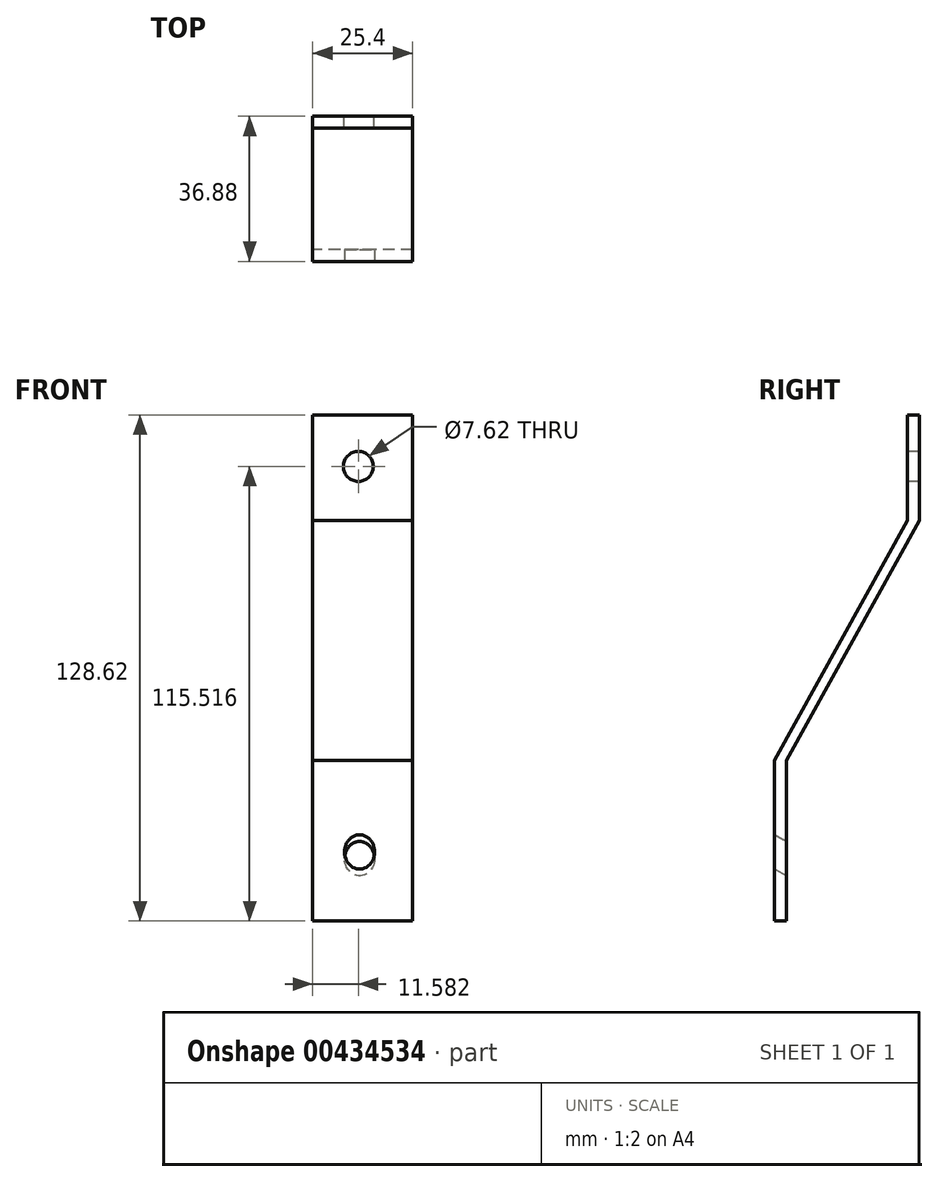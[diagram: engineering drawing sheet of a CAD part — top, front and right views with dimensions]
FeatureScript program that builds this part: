
annotation { "Feature Type Name" : "Feature", "Feature Type Description" : "" }
export const myFeature = defineFeature(function(context is Context, id is Id, definition is map)
    precondition{}
    {
        {
            var Q0;
            Q0=qCreatedBy(makeId("Right.planeOp"),FACE);
            var sketch = newSketch(context, id + "F0", { "sketchPlane" : qUnion([Q0])});
            skLineSegment(sketch, "E0.bottom", {"start": v(-49.07, -10.82) * mm, "end": v(-46.02, -10.82) * mm});
            skLineSegment(sketch, "E0.top", {"start": v(-49.07, -51.66) * mm, "end": v(-46.02, -51.66) * mm});
            skLineSegment(sketch, "E0.left", {"start": v(-49.07, -10.82) * mm, "end": v(-49.07, -51.66) * mm});
            skLineSegment(sketch, "E0.right", {"start": v(-46.02, -10.82) * mm, "end": v(-46.02, -51.66) * mm});
            skPoint(sketch, "E0.middle", {"position": v(-47.55, -31.24) * mm});
            skLineSegment(sketch, "E1", {"start": v(-49.07, -10.82) * mm, "end": v(-15.24, 50.14) * mm});
            skLineSegment(sketch, "E2", {"start": v(-46.02, -10.82) * mm, "end": v(-12.2, 50.14) * mm});
            skLineSegment(sketch, "E3", {"start": v(-12.2, 50.14) * mm, "end": v(-12.2, 76.96) * mm});
            skLineSegment(sketch, "E4", {"start": v(-12.2, 76.96) * mm, "end": v(-15.24, 76.96) * mm});
            skLineSegment(sketch, "E5", {"start": v(-15.24, 76.96) * mm, "end": v(-15.24, 50.14) * mm});
            skSolve(sketch);
        }
        {
            var Q0;
            Q0 = qSketchRegion(id + "F0", true);
            extrude(context, id + "F1", {"entities" : qUnion([Q0]), "depth" : 25.4 * mm});
        }
        {
            var Q0;
            Q0=makeQuery(id+"F1.opExtrude","SWEPT_FACE",FACE,{"disambiguationData":[OSD([sQuery(id+"F0.wireOp",EDGE,"E1")])]});
            var sketch = newSketch(context, id + "F2", { "sketchPlane" : qUnion([Q0])});
            skCircle(sketch, "E6", {"center": v(11.89, -53.62) * mm, "radius": 3.23 * mm});
            skSolve(sketch);
        }
        {
            var Q0;
            Q0=sQuery(id+"F2.wireOp",VERTEX,"E6.center");
            var Q1;
            Q1=makeQuery(id+"F1.opExtrude","SWEPT_BODY",BODY,{"disambiguationData":[OSD([sQuery(id+"F0.wireOp",EDGE,"E0.top"),sQuery(id+"F0.wireOp",EDGE,"E0.left"),sQuery(id+"F0.wireOp",EDGE,"E0.right"),sQuery(id+"F0.wireOp",EDGE,"E1"),sQuery(id+"F0.wireOp",EDGE,"E2"),sQuery(id+"F0.wireOp",EDGE,"E3"),sQuery(id+"F0.wireOp",EDGE,"E4"),sQuery(id+"F0.wireOp",EDGE,"E5")])]});
            hole(context, id + "F3", {"style" : HoleStyle.SIMPLE, "endStyle" : HoleEndStyle.THROUGH, "holeDiameter" : 7.62 * mm, "isTappedThrough" : true, "tappedDepth" : 12.7 * mm, "tapClearance" : 3, "locations" : qUnion([Q0]), "scope" : qUnion([Q1])});
        }
        {
            var Q0;
            Q0=makeQuery(id+"F1.opExtrude","SWEPT_FACE",FACE,{"disambiguationData":[OSD([sQuery(id+"F0.wireOp",EDGE,"E5")])]});
            var sketch = newSketch(context, id + "F4", { "sketchPlane" : qUnion([Q0])});
            skCircle(sketch, "E7", {"center": v(11.58, 63.86) * mm, "radius": 3.81 * mm});
            skSolve(sketch);
        }
        {
            var Q0;
            Q0=sQuery(id+"F4.wireOp",VERTEX,"E7.center");
            var Q1;
            Q1=makeQuery(id+"F1.opExtrude","SWEPT_BODY",BODY,{"disambiguationData":[OSD([sQuery(id+"F0.wireOp",EDGE,"E0.top"),sQuery(id+"F0.wireOp",EDGE,"E0.left"),sQuery(id+"F0.wireOp",EDGE,"E0.right"),sQuery(id+"F0.wireOp",EDGE,"E1"),sQuery(id+"F0.wireOp",EDGE,"E2"),sQuery(id+"F0.wireOp",EDGE,"E3"),sQuery(id+"F0.wireOp",EDGE,"E4"),sQuery(id+"F0.wireOp",EDGE,"E5")])]});
            hole(context, id + "F5", {"style" : HoleStyle.SIMPLE, "endStyle" : HoleEndStyle.THROUGH, "holeDiameter" : 7.62 * mm, "isTappedThrough" : true, "tappedDepth" : 12.7 * mm, "tapClearance" : 3, "locations" : qUnion([Q0]), "scope" : qUnion([Q1])});
        }
    });
